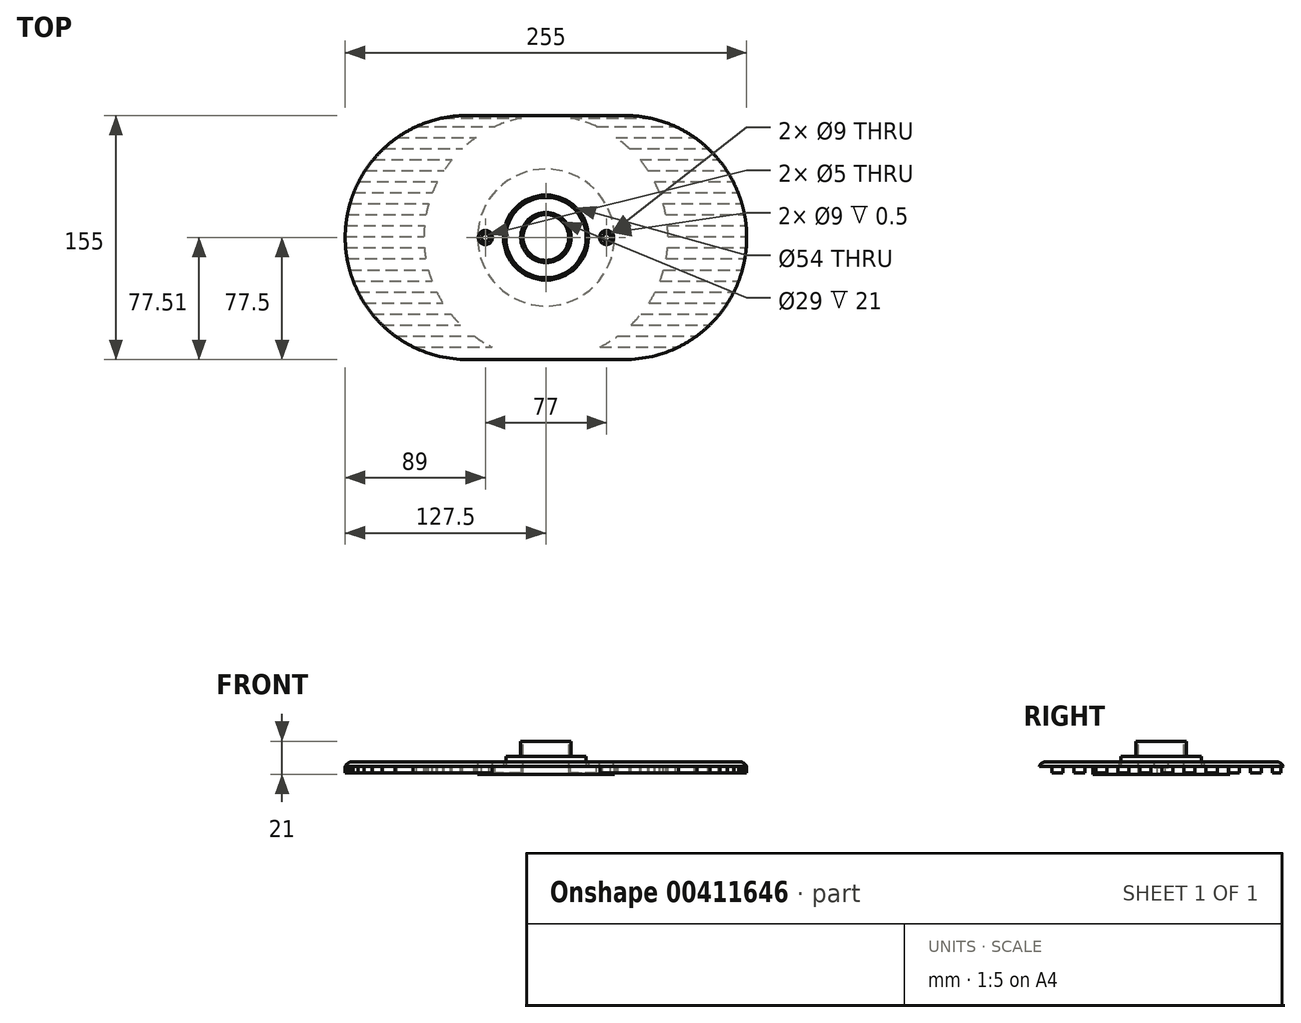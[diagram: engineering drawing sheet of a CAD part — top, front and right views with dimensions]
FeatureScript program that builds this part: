
annotation { "Feature Type Name" : "Feature", "Feature Type Description" : "" }
export const myFeature = defineFeature(function(context is Context, id is Id, definition is map)
    precondition{}
    {
        {
            var Q0;
            Q0=qCreatedBy(makeId("Top.planeOp"),FACE);
            var sketch = newSketch(context, id + "F0", { "sketchPlane" : qUnion([Q0])});
            skCircle(sketch, "E0", {"center": v(0, 0) * mm, "radius": 25.5 * mm});
            skCircle(sketch, "E1", {"center": v(0, 0.01) * mm, "radius": 14.5 * mm});
            skCircle(sketch, "E2", {"center": v(0, 0) * mm, "radius": 77.5 * mm});
            skCircle(sketch, "E3", {"center": v(0, 0) * mm, "radius": 16 * mm});
            skLineSegment(sketch, "E4", {"start": v(0, 77.5) * mm, "end": v(50, 77.5) * mm});
            skLineSegment(sketch, "E5", {"start": v(0, 77.5) * mm, "end": v(-50, 77.5) * mm});
            skLineSegment(sketch, "E6", {"start": v(0, -77.5) * mm, "end": v(-50, -77.5) * mm});
            skLineSegment(sketch, "E7", {"start": v(0, -77.5) * mm, "end": v(50, -77.5) * mm});
            skArc(sketch, "E8", {"start": v(-50, 77.5) * mm, "mid": v(-127.5, 0) * mm, "end": v(-50, -77.5) * mm});
            skLineSegment(sketch, "E9", {"start": v(0, 0) * mm, "end": v(0, 99.89) * mm, "construction": true});
            skArc(sketch, "E10.MirrorCS", {"start": v(50, 77.5) * mm, "mid": v(127.5, 0) * mm, "end": v(50, -77.5) * mm});
            skCircle(sketch, "E11", {"center": v(0, 0.01) * mm, "radius": 27 * mm});
            skEllipse(sketch, "E12", {"center": v(0, 0.01) * mm, "majorRadius": 43.5 * mm, "minorRadius": 43.5 * mm, "majorAxis": v(-1, 0)});
            skLineSegment(sketch, "E13.0.1.0", {"start": v(-94.43, 63.5) * mm, "end": v(-44.43, 63.5) * mm});
            skLineSegment(sketch, "E13.0.2.0", {"start": v(-103.05, 56.5) * mm, "end": v(-53.05, 56.5) * mm});
            skLineSegment(sketch, "E13.0.3.0", {"start": v(-109.63, 49.5) * mm, "end": v(-59.63, 49.5) * mm});
            skLineSegment(sketch, "E13.0.4.0", {"start": v(-114.8, 42.5) * mm, "end": v(-64.8, 42.5) * mm});
            skLineSegment(sketch, "E13.0.5.0", {"start": v(-118.9, 35.5) * mm, "end": v(-68.9, 35.5) * mm});
            skLineSegment(sketch, "E13.0.6.0", {"start": v(-122.07, 28.5) * mm, "end": v(-72.07, 28.5) * mm});
            skLineSegment(sketch, "E13.0.7.0", {"start": v(-124.46, 21.5) * mm, "end": v(-74.46, 21.5) * mm});
            skLineSegment(sketch, "E13.0.8.0", {"start": v(-126.13, 14.5) * mm, "end": v(-76.13, 14.5) * mm});
            skLineSegment(sketch, "E13.0.9.0", {"start": v(-127.14, 7.5) * mm, "end": v(-77.14, 7.5) * mm});
            skLineSegment(sketch, "E13.0.10.0", {"start": v(-127.5, 0.5) * mm, "end": v(-77.5, 0.5) * mm});
            skLineSegment(sketch, "E13.0.11.0", {"start": v(-127.23, -6.5) * mm, "end": v(-77.23, -6.5) * mm});
            skLineSegment(sketch, "E13.0.12.0", {"start": v(-126.32, -13.5) * mm, "end": v(-76.32, -13.5) * mm});
            skLineSegment(sketch, "E13.0.13.0", {"start": v(-124.74, -20.5) * mm, "end": v(-74.74, -20.5) * mm});
            skLineSegment(sketch, "E13.0.14.0", {"start": v(-122.46, -27.5) * mm, "end": v(-72.46, -27.5) * mm});
            skLineSegment(sketch, "E13.0.15.0", {"start": v(-119.4, -34.5) * mm, "end": v(-69.4, -34.5) * mm});
            skLineSegment(sketch, "E13.0.16.0", {"start": v(-115.45, -41.5) * mm, "end": v(-65.45, -41.5) * mm});
            skLineSegment(sketch, "E13.0.17.0", {"start": v(-110.45, -48.5) * mm, "end": v(-60.45, -48.5) * mm});
            skLineSegment(sketch, "E13.0.18.0", {"start": v(-104.1, -55.5) * mm, "end": v(-54.1, -55.5) * mm});
            skLineSegment(sketch, "E13.0.19.0", {"start": v(-95.83, -62.5) * mm, "end": v(-45.83, -62.5) * mm});
            skLineSegment(sketch, "E13.0.20.0", {"start": v(-84.3, -69.5) * mm, "end": v(-34.3, -69.5) * mm});
            skLineSegment(sketch, "E14.trimOffspring", {"start": v(32.19, 70.5) * mm, "end": v(82.19, 70.5) * mm});
            skLineSegment(sketch, "E15.trimOffspring", {"start": v(44.43, 63.5) * mm, "end": v(94.43, 63.5) * mm});
            skLineSegment(sketch, "E16.trimOffspring", {"start": v(53.05, 56.5) * mm, "end": v(103.05, 56.5) * mm});
            skLineSegment(sketch, "E17.trimOffspring", {"start": v(59.63, 49.5) * mm, "end": v(109.63, 49.5) * mm});
            skLineSegment(sketch, "E18.trimOffspring", {"start": v(64.8, 42.5) * mm, "end": v(114.8, 42.5) * mm});
            skLineSegment(sketch, "E19.trimOffspring", {"start": v(68.9, 35.5) * mm, "end": v(118.9, 35.5) * mm});
            skLineSegment(sketch, "E20.trimOffspring", {"start": v(72.07, 28.5) * mm, "end": v(122.07, 28.5) * mm});
            skLineSegment(sketch, "E21.trimOffspring", {"start": v(74.46, 21.5) * mm, "end": v(124.46, 21.5) * mm});
            skLineSegment(sketch, "E22.trimOffspring", {"start": v(76.13, 14.5) * mm, "end": v(126.13, 14.5) * mm});
            skLineSegment(sketch, "E23.trimOffspring", {"start": v(77.14, 7.5) * mm, "end": v(127.14, 7.5) * mm});
            skLineSegment(sketch, "E24.trimOffspring", {"start": v(77.5, 0.5) * mm, "end": v(127.5, 0.5) * mm});
            skLineSegment(sketch, "E25.trimOffspring", {"start": v(77.23, -6.5) * mm, "end": v(127.23, -6.5) * mm});
            skLineSegment(sketch, "E26.trimOffspring", {"start": v(76.32, -13.5) * mm, "end": v(126.32, -13.5) * mm});
            skLineSegment(sketch, "E27.trimOffspring", {"start": v(74.74, -20.5) * mm, "end": v(124.74, -20.5) * mm});
            skLineSegment(sketch, "E28.trimOffspring", {"start": v(72.46, -27.5) * mm, "end": v(122.46, -27.5) * mm});
            skLineSegment(sketch, "E29.trimOffspring", {"start": v(69.4, -34.5) * mm, "end": v(119.4, -34.5) * mm});
            skLineSegment(sketch, "E30.trimOffspring", {"start": v(65.45, -41.5) * mm, "end": v(115.45, -41.5) * mm});
            skLineSegment(sketch, "E31.trimOffspring", {"start": v(60.45, -48.5) * mm, "end": v(110.45, -48.5) * mm});
            skLineSegment(sketch, "E32.trimOffspring", {"start": v(54.1, -55.5) * mm, "end": v(104.1, -55.5) * mm});
            skLineSegment(sketch, "E33.trimOffspring", {"start": v(45.83, -62.5) * mm, "end": v(95.83, -62.5) * mm});
            skLineSegment(sketch, "E34.trimOffspring", {"start": v(34.3, -69.5) * mm, "end": v(84.3, -69.5) * mm});
            skLineSegment(sketch, "E35.trimOffspring", {"start": v(-82.19, 70.5) * mm, "end": v(-32.19, 70.5) * mm});
            skLineSegment(sketch, "E36", {"start": v(-65.46, 75.94) * mm, "end": v(-15.46, 75.94) * mm});
            skLineSegment(sketch, "E37.trimOffspring", {"start": v(15.46, 75.94) * mm, "end": v(65.46, 75.94) * mm});
            skLineSegment(sketch, "E38", {"start": v(0, 0.01) * mm, "end": v(-38.5, 0.01) * mm, "construction": true});
            skLineSegment(sketch, "E39", {"start": v(0, 0.01) * mm, "end": v(38.5, 0.01) * mm, "construction": true});
            skSolve(sketch);
        }
        {
            var Q0;
            Q0=makeQuery(id+"F0.imprint","IMPRINT",FACE,{"disambiguationData":[TD([[makeQuery(id+"F0.imprint","IMPRINT",EDGE,{"derivedFrom":sQuery(id+"F0.wireOp",EDGE,"E11")}),-1.0]])]});
            var Q1;
            Q1=makeQuery(id+"F0.imprint","IMPRINT",FACE,{"disambiguationData":[TD([[makeQuery(id+"F0.imprint","IMPRINT",EDGE,{"derivedFrom":sQuery(id+"F0.wireOp",EDGE,"E0")}),-1.0]])]});
            var Q2;
            Q2=makeQuery(id+"F0.imprint","IMPRINT",FACE,{"disambiguationData":[TD([[makeQuery(id+"F0.imprint","IMPRINT",EDGE,{"derivedFrom":sQuery(id+"F0.wireOp",EDGE,"E0")}),1.0]])]});
            var Q3;
            Q3=makeQuery(id+"F0.imprint","IMPRINT",FACE,{"disambiguationData":[TD([[makeQuery(id+"F0.imprint","IMPRINT",EDGE,{"derivedFrom":sQuery(id+"F0.wireOp",EDGE,"E1")}),-1.0]])]});
            extrude(context, id + "F1", {"entities" : qUnion([Q0, Q1, Q2, Q3]), "oppositeDirection" : true, "depth" : 5 * mm});
        }
        {
            var Q0;
            Q0=makeQuery(id+"F0.imprint","IMPRINT",FACE,{"disambiguationData":[TD([[makeQuery(id+"F0.imprint","IMPRINT",EDGE,{"derivedFrom":sQuery(id+"F0.wireOp",EDGE,"E0")}),1.0]])]});
            extrude(context, id + "F2", {"entities" : qUnion([Q0]), "operationType" : NewBodyOperationType.ADD, "depth" : 6.5 * mm});
        }
        {
            var Q0;
            Q0=makeQuery(id+"F0.imprint","IMPRINT",FACE,{"disambiguationData":[TD([[makeQuery(id+"F0.imprint","IMPRINT",EDGE,{"derivedFrom":sQuery(id+"F0.wireOp",EDGE,"E1")}),-1.0]])]});
            extrude(context, id + "F3", {"entities" : qUnion([Q0]), "operationType" : NewBodyOperationType.ADD, "depth" : 16 * mm});
        }
        {
            var Q0;
            Q0=makeQuery(id+"F0.imprint","IMPRINT",FACE,{"disambiguationData":[TD([[makeQuery(id+"F0.imprint","IMPRINT",EDGE,{"derivedFrom":sQuery(id+"F0.wireOp",EDGE,"E12")}),-1.0]])]});
            var Q1;
            Q1=makeQuery(id+"F0.imprint","IMPRINT",FACE,{"disambiguationData":[TD([[makeQuery(id+"F0.imprint","IMPRINT",EDGE,{"derivedFrom":sQuery(id+"F0.wireOp",EDGE,"E11")}),-1.0]])]});
            var Q2;
            {var subQ0=sQuery(id+"F0.wireOp",EDGE,"E5");Q2=makeQuery(id+"F0.imprint","IMPRINT",FACE,{"disambiguationData":[TD([[makeQuery(id+"F0.imprint","IMPRINT",EDGE,{"derivedFrom":subQ0}),1.0]])]});}
            var Q3;
            {var subQ0=sQuery(id+"F0.wireOp",EDGE,"E13.0.1.0");Q3=makeQuery(id+"F0.imprint","IMPRINT",FACE,{"disambiguationData":[TD([[makeQuery(id+"F0.imprint","IMPRINT",EDGE,{"derivedFrom":subQ0}),1.0]])]});}
            var Q4;
            {var subQ0=sQuery(id+"F0.wireOp",EDGE,"E13.0.1.0");Q4=makeQuery(id+"F0.imprint","IMPRINT",FACE,{"disambiguationData":[TD([[makeQuery(id+"F0.imprint","IMPRINT",EDGE,{"derivedFrom":subQ0}),-1.0]])]});}
            var Q5;
            {var subQ0=sQuery(id+"F0.wireOp",EDGE,"E13.0.2.0");Q5=makeQuery(id+"F0.imprint","IMPRINT",FACE,{"disambiguationData":[TD([[makeQuery(id+"F0.imprint","IMPRINT",EDGE,{"derivedFrom":subQ0}),-1.0]])]});}
            var Q6;
            {var subQ0=sQuery(id+"F0.wireOp",EDGE,"E13.0.3.0");Q6=makeQuery(id+"F0.imprint","IMPRINT",FACE,{"disambiguationData":[TD([[makeQuery(id+"F0.imprint","IMPRINT",EDGE,{"derivedFrom":subQ0}),-1.0]])]});}
            var Q7;
            {var subQ0=sQuery(id+"F0.wireOp",EDGE,"E13.0.4.0");Q7=makeQuery(id+"F0.imprint","IMPRINT",FACE,{"disambiguationData":[TD([[makeQuery(id+"F0.imprint","IMPRINT",EDGE,{"derivedFrom":subQ0}),-1.0]])]});}
            var Q8;
            {var subQ0=sQuery(id+"F0.wireOp",EDGE,"E13.0.5.0");Q8=makeQuery(id+"F0.imprint","IMPRINT",FACE,{"disambiguationData":[TD([[makeQuery(id+"F0.imprint","IMPRINT",EDGE,{"derivedFrom":subQ0}),-1.0]])]});}
            var Q9;
            {var subQ0=sQuery(id+"F0.wireOp",EDGE,"E13.0.6.0");Q9=makeQuery(id+"F0.imprint","IMPRINT",FACE,{"disambiguationData":[TD([[makeQuery(id+"F0.imprint","IMPRINT",EDGE,{"derivedFrom":subQ0}),-1.0]])]});}
            var Q10;
            {var subQ0=sQuery(id+"F0.wireOp",EDGE,"E13.0.7.0");Q10=makeQuery(id+"F0.imprint","IMPRINT",FACE,{"disambiguationData":[TD([[makeQuery(id+"F0.imprint","IMPRINT",EDGE,{"derivedFrom":subQ0}),-1.0]])]});}
            var Q11;
            {var subQ0=sQuery(id+"F0.wireOp",EDGE,"E13.0.8.0");Q11=makeQuery(id+"F0.imprint","IMPRINT",FACE,{"disambiguationData":[TD([[makeQuery(id+"F0.imprint","IMPRINT",EDGE,{"derivedFrom":subQ0}),-1.0]])]});}
            var Q12;
            {var subQ0=sQuery(id+"F0.wireOp",EDGE,"E13.0.9.0");Q12=makeQuery(id+"F0.imprint","IMPRINT",FACE,{"disambiguationData":[TD([[makeQuery(id+"F0.imprint","IMPRINT",EDGE,{"derivedFrom":subQ0}),-1.0]])]});}
            var Q13;
            {var subQ0=sQuery(id+"F0.wireOp",EDGE,"E13.0.10.0");Q13=makeQuery(id+"F0.imprint","IMPRINT",FACE,{"disambiguationData":[TD([[makeQuery(id+"F0.imprint","IMPRINT",EDGE,{"derivedFrom":subQ0}),-1.0]])]});}
            var Q14;
            {var subQ0=sQuery(id+"F0.wireOp",EDGE,"E13.0.11.0");Q14=makeQuery(id+"F0.imprint","IMPRINT",FACE,{"disambiguationData":[TD([[makeQuery(id+"F0.imprint","IMPRINT",EDGE,{"derivedFrom":subQ0}),-1.0]])]});}
            var Q15;
            {var subQ0=sQuery(id+"F0.wireOp",EDGE,"E13.0.12.0");Q15=makeQuery(id+"F0.imprint","IMPRINT",FACE,{"disambiguationData":[TD([[makeQuery(id+"F0.imprint","IMPRINT",EDGE,{"derivedFrom":subQ0}),-1.0]])]});}
            var Q16;
            {var subQ0=sQuery(id+"F0.wireOp",EDGE,"E13.0.13.0");Q16=makeQuery(id+"F0.imprint","IMPRINT",FACE,{"disambiguationData":[TD([[makeQuery(id+"F0.imprint","IMPRINT",EDGE,{"derivedFrom":subQ0}),-1.0]])]});}
            var Q17;
            {var subQ0=sQuery(id+"F0.wireOp",EDGE,"E13.0.15.0");Q17=makeQuery(id+"F0.imprint","IMPRINT",FACE,{"disambiguationData":[TD([[makeQuery(id+"F0.imprint","IMPRINT",EDGE,{"derivedFrom":subQ0}),-1.0]])]});}
            var Q18;
            {var subQ0=sQuery(id+"F0.wireOp",EDGE,"E13.0.16.0");Q18=makeQuery(id+"F0.imprint","IMPRINT",FACE,{"disambiguationData":[TD([[makeQuery(id+"F0.imprint","IMPRINT",EDGE,{"derivedFrom":subQ0}),-1.0]])]});}
            var Q19;
            {var subQ0=sQuery(id+"F0.wireOp",EDGE,"E13.0.17.0");Q19=makeQuery(id+"F0.imprint","IMPRINT",FACE,{"disambiguationData":[TD([[makeQuery(id+"F0.imprint","IMPRINT",EDGE,{"derivedFrom":subQ0}),-1.0]])]});}
            var Q20;
            {var subQ0=sQuery(id+"F0.wireOp",EDGE,"E13.0.18.0");Q20=makeQuery(id+"F0.imprint","IMPRINT",FACE,{"disambiguationData":[TD([[makeQuery(id+"F0.imprint","IMPRINT",EDGE,{"derivedFrom":subQ0}),-1.0]])]});}
            var Q21;
            {var subQ0=sQuery(id+"F0.wireOp",EDGE,"E13.0.19.0");Q21=makeQuery(id+"F0.imprint","IMPRINT",FACE,{"disambiguationData":[TD([[makeQuery(id+"F0.imprint","IMPRINT",EDGE,{"derivedFrom":subQ0}),-1.0]])]});}
            var Q22;
            {var subQ0=sQuery(id+"F0.wireOp",EDGE,"E6");Q22=makeQuery(id+"F0.imprint","IMPRINT",FACE,{"disambiguationData":[TD([[makeQuery(id+"F0.imprint","IMPRINT",EDGE,{"derivedFrom":subQ0}),-1.0]])]});}
            var Q23;
            {var subQ0=sQuery(id+"F0.wireOp",EDGE,"E13.0.14.0");Q23=makeQuery(id+"F0.imprint","IMPRINT",FACE,{"disambiguationData":[TD([[makeQuery(id+"F0.imprint","IMPRINT",EDGE,{"derivedFrom":subQ0}),-1.0]])]});}
            var Q24;
            {var subQ0=sQuery(id+"F0.wireOp",EDGE,"E7");Q24=makeQuery(id+"F0.imprint","IMPRINT",FACE,{"disambiguationData":[TD([[makeQuery(id+"F0.imprint","IMPRINT",EDGE,{"derivedFrom":subQ0}),1.0]])]});}
            var Q25;
            {var subQ0=sQuery(id+"F0.wireOp",EDGE,"E33.trimOffspring");Q25=makeQuery(id+"F0.imprint","IMPRINT",FACE,{"disambiguationData":[TD([[makeQuery(id+"F0.imprint","IMPRINT",EDGE,{"derivedFrom":subQ0}),-1.0]])]});}
            var Q26;
            {var subQ0=sQuery(id+"F0.wireOp",EDGE,"E32.trimOffspring");Q26=makeQuery(id+"F0.imprint","IMPRINT",FACE,{"disambiguationData":[TD([[makeQuery(id+"F0.imprint","IMPRINT",EDGE,{"derivedFrom":subQ0}),-1.0]])]});}
            var Q27;
            {var subQ0=sQuery(id+"F0.wireOp",EDGE,"E31.trimOffspring");Q27=makeQuery(id+"F0.imprint","IMPRINT",FACE,{"disambiguationData":[TD([[makeQuery(id+"F0.imprint","IMPRINT",EDGE,{"derivedFrom":subQ0}),-1.0]])]});}
            var Q28;
            {var subQ0=sQuery(id+"F0.wireOp",EDGE,"E30.trimOffspring");Q28=makeQuery(id+"F0.imprint","IMPRINT",FACE,{"disambiguationData":[TD([[makeQuery(id+"F0.imprint","IMPRINT",EDGE,{"derivedFrom":subQ0}),-1.0]])]});}
            var Q29;
            {var subQ0=sQuery(id+"F0.wireOp",EDGE,"E29.trimOffspring");Q29=makeQuery(id+"F0.imprint","IMPRINT",FACE,{"disambiguationData":[TD([[makeQuery(id+"F0.imprint","IMPRINT",EDGE,{"derivedFrom":subQ0}),-1.0]])]});}
            var Q30;
            {var subQ0=sQuery(id+"F0.wireOp",EDGE,"E28.trimOffspring");Q30=makeQuery(id+"F0.imprint","IMPRINT",FACE,{"disambiguationData":[TD([[makeQuery(id+"F0.imprint","IMPRINT",EDGE,{"derivedFrom":subQ0}),-1.0]])]});}
            var Q31;
            {var subQ0=sQuery(id+"F0.wireOp",EDGE,"E27.trimOffspring");Q31=makeQuery(id+"F0.imprint","IMPRINT",FACE,{"disambiguationData":[TD([[makeQuery(id+"F0.imprint","IMPRINT",EDGE,{"derivedFrom":subQ0}),-1.0]])]});}
            var Q32;
            {var subQ0=sQuery(id+"F0.wireOp",EDGE,"E26.trimOffspring");Q32=makeQuery(id+"F0.imprint","IMPRINT",FACE,{"disambiguationData":[TD([[makeQuery(id+"F0.imprint","IMPRINT",EDGE,{"derivedFrom":subQ0}),-1.0]])]});}
            var Q33;
            {var subQ0=sQuery(id+"F0.wireOp",EDGE,"E25.trimOffspring");Q33=makeQuery(id+"F0.imprint","IMPRINT",FACE,{"disambiguationData":[TD([[makeQuery(id+"F0.imprint","IMPRINT",EDGE,{"derivedFrom":subQ0}),-1.0]])]});}
            var Q34;
            {var subQ0=sQuery(id+"F0.wireOp",EDGE,"E24.trimOffspring");Q34=makeQuery(id+"F0.imprint","IMPRINT",FACE,{"disambiguationData":[TD([[makeQuery(id+"F0.imprint","IMPRINT",EDGE,{"derivedFrom":subQ0}),-1.0]])]});}
            var Q35;
            {var subQ0=sQuery(id+"F0.wireOp",EDGE,"E23.trimOffspring");Q35=makeQuery(id+"F0.imprint","IMPRINT",FACE,{"disambiguationData":[TD([[makeQuery(id+"F0.imprint","IMPRINT",EDGE,{"derivedFrom":subQ0}),-1.0]])]});}
            var Q36;
            {var subQ0=sQuery(id+"F0.wireOp",EDGE,"E22.trimOffspring");Q36=makeQuery(id+"F0.imprint","IMPRINT",FACE,{"disambiguationData":[TD([[makeQuery(id+"F0.imprint","IMPRINT",EDGE,{"derivedFrom":subQ0}),-1.0]])]});}
            var Q37;
            {var subQ0=sQuery(id+"F0.wireOp",EDGE,"E21.trimOffspring");Q37=makeQuery(id+"F0.imprint","IMPRINT",FACE,{"disambiguationData":[TD([[makeQuery(id+"F0.imprint","IMPRINT",EDGE,{"derivedFrom":subQ0}),-1.0]])]});}
            var Q38;
            {var subQ0=sQuery(id+"F0.wireOp",EDGE,"E20.trimOffspring");Q38=makeQuery(id+"F0.imprint","IMPRINT",FACE,{"disambiguationData":[TD([[makeQuery(id+"F0.imprint","IMPRINT",EDGE,{"derivedFrom":subQ0}),-1.0]])]});}
            var Q39;
            {var subQ0=sQuery(id+"F0.wireOp",EDGE,"E19.trimOffspring");Q39=makeQuery(id+"F0.imprint","IMPRINT",FACE,{"disambiguationData":[TD([[makeQuery(id+"F0.imprint","IMPRINT",EDGE,{"derivedFrom":subQ0}),-1.0]])]});}
            var Q40;
            {var subQ0=sQuery(id+"F0.wireOp",EDGE,"E18.trimOffspring");Q40=makeQuery(id+"F0.imprint","IMPRINT",FACE,{"disambiguationData":[TD([[makeQuery(id+"F0.imprint","IMPRINT",EDGE,{"derivedFrom":subQ0}),-1.0]])]});}
            var Q41;
            {var subQ0=sQuery(id+"F0.wireOp",EDGE,"E17.trimOffspring");Q41=makeQuery(id+"F0.imprint","IMPRINT",FACE,{"disambiguationData":[TD([[makeQuery(id+"F0.imprint","IMPRINT",EDGE,{"derivedFrom":subQ0}),-1.0]])]});}
            var Q42;
            {var subQ0=sQuery(id+"F0.wireOp",EDGE,"E4");Q42=makeQuery(id+"F0.imprint","IMPRINT",FACE,{"disambiguationData":[TD([[makeQuery(id+"F0.imprint","IMPRINT",EDGE,{"derivedFrom":subQ0}),-1.0]])]});}
            var Q43;
            {var subQ0=sQuery(id+"F0.wireOp",EDGE,"E14.trimOffspring");Q43=makeQuery(id+"F0.imprint","IMPRINT",FACE,{"disambiguationData":[TD([[makeQuery(id+"F0.imprint","IMPRINT",EDGE,{"derivedFrom":subQ0}),-1.0]])]});}
            var Q44;
            {var subQ0=sQuery(id+"F0.wireOp",EDGE,"E15.trimOffspring");Q44=makeQuery(id+"F0.imprint","IMPRINT",FACE,{"disambiguationData":[TD([[makeQuery(id+"F0.imprint","IMPRINT",EDGE,{"derivedFrom":subQ0}),-1.0]])]});}
            var Q45;
            {var subQ0=sQuery(id+"F0.wireOp",EDGE,"E16.trimOffspring");Q45=makeQuery(id+"F0.imprint","IMPRINT",FACE,{"disambiguationData":[TD([[makeQuery(id+"F0.imprint","IMPRINT",EDGE,{"derivedFrom":subQ0}),-1.0]])]});}
            var Q46;
            {var subQ0=sQuery(id+"F0.wireOp",EDGE,"E35.trimOffspring");Q46=makeQuery(id+"F0.imprint","IMPRINT",FACE,{"disambiguationData":[TD([[makeQuery(id+"F0.imprint","IMPRINT",EDGE,{"derivedFrom":subQ0}),1.0]])]});}
            var Q47;
            {var subQ0=sQuery(id+"F0.wireOp",EDGE,"E14.trimOffspring");Q47=makeQuery(id+"F0.imprint","IMPRINT",FACE,{"disambiguationData":[TD([[makeQuery(id+"F0.imprint","IMPRINT",EDGE,{"derivedFrom":subQ0}),1.0]])]});}
            extrude(context, id + "F4", {"entities" : qUnion([Q0, Q1, Q2, Q3, Q4, Q5, Q6, Q7, Q8, Q9, Q10, Q11, Q12, Q13, Q14, Q15, Q16, Q17, Q18, Q19, Q20, Q21, Q22, Q23, Q24, Q25, Q26, Q27, Q28, Q29, Q30, Q31, Q32, Q33, Q34, Q35, Q36, Q37, Q38, Q39, Q40, Q41, Q42, Q43, Q44, Q45, Q46, Q47]), "depth" : 3 * mm});
        }
        {
            var Q0;
            Q0=makeQuery(id+"F4.opExtrude","CAP_EDGE",EDGE,{"disambiguationData":[OSD([sQuery(id+"F0.wireOp",EDGE,"E6"),sQuery(id+"F0.wireOp",EDGE,"E7")])],"isStart":false});
            fillet(context, id + "F5", {"entities" : qUnion([Q0]), "radius" : 5 * mm, "tangentPropagation" : true, "allowEdgeOverflow" : false});
        }
        {
            var Q0;
            {var subQ0=sQuery(id+"F0.wireOp",EDGE,"E13.0.19.0");Q0=makeQuery(id+"F0.imprint","IMPRINT",FACE,{"disambiguationData":[TD([[makeQuery(id+"F0.imprint","IMPRINT",EDGE,{"derivedFrom":subQ0}),-1.0]])]});}
            var Q1;
            {var subQ0=sQuery(id+"F0.wireOp",EDGE,"E13.0.17.0");Q1=makeQuery(id+"F0.imprint","IMPRINT",FACE,{"disambiguationData":[TD([[makeQuery(id+"F0.imprint","IMPRINT",EDGE,{"derivedFrom":subQ0}),-1.0]])]});}
            var Q2;
            {var subQ0=sQuery(id+"F0.wireOp",EDGE,"E13.0.15.0");Q2=makeQuery(id+"F0.imprint","IMPRINT",FACE,{"disambiguationData":[TD([[makeQuery(id+"F0.imprint","IMPRINT",EDGE,{"derivedFrom":subQ0}),-1.0]])]});}
            var Q3;
            {var subQ0=sQuery(id+"F0.wireOp",EDGE,"E13.0.13.0");Q3=makeQuery(id+"F0.imprint","IMPRINT",FACE,{"disambiguationData":[TD([[makeQuery(id+"F0.imprint","IMPRINT",EDGE,{"derivedFrom":subQ0}),-1.0]])]});}
            var Q4;
            {var subQ0=sQuery(id+"F0.wireOp",EDGE,"E13.0.11.0");Q4=makeQuery(id+"F0.imprint","IMPRINT",FACE,{"disambiguationData":[TD([[makeQuery(id+"F0.imprint","IMPRINT",EDGE,{"derivedFrom":subQ0}),-1.0]])]});}
            var Q5;
            {var subQ0=sQuery(id+"F0.wireOp",EDGE,"E13.0.9.0");Q5=makeQuery(id+"F0.imprint","IMPRINT",FACE,{"disambiguationData":[TD([[makeQuery(id+"F0.imprint","IMPRINT",EDGE,{"derivedFrom":subQ0}),-1.0]])]});}
            var Q6;
            {var subQ0=sQuery(id+"F0.wireOp",EDGE,"E13.0.7.0");Q6=makeQuery(id+"F0.imprint","IMPRINT",FACE,{"disambiguationData":[TD([[makeQuery(id+"F0.imprint","IMPRINT",EDGE,{"derivedFrom":subQ0}),-1.0]])]});}
            var Q7;
            {var subQ0=sQuery(id+"F0.wireOp",EDGE,"E13.0.5.0");Q7=makeQuery(id+"F0.imprint","IMPRINT",FACE,{"disambiguationData":[TD([[makeQuery(id+"F0.imprint","IMPRINT",EDGE,{"derivedFrom":subQ0}),-1.0]])]});}
            var Q8;
            {var subQ0=sQuery(id+"F0.wireOp",EDGE,"E13.0.3.0");Q8=makeQuery(id+"F0.imprint","IMPRINT",FACE,{"disambiguationData":[TD([[makeQuery(id+"F0.imprint","IMPRINT",EDGE,{"derivedFrom":subQ0}),-1.0]])]});}
            var Q9;
            {var subQ0=sQuery(id+"F0.wireOp",EDGE,"E13.0.1.0");Q9=makeQuery(id+"F0.imprint","IMPRINT",FACE,{"disambiguationData":[TD([[makeQuery(id+"F0.imprint","IMPRINT",EDGE,{"derivedFrom":subQ0}),-1.0]])]});}
            var Q10;
            {var subQ0=sQuery(id+"F0.wireOp",EDGE,"E15.trimOffspring");Q10=makeQuery(id+"F0.imprint","IMPRINT",FACE,{"disambiguationData":[TD([[makeQuery(id+"F0.imprint","IMPRINT",EDGE,{"derivedFrom":subQ0}),-1.0]])]});}
            var Q11;
            {var subQ0=sQuery(id+"F0.wireOp",EDGE,"E17.trimOffspring");Q11=makeQuery(id+"F0.imprint","IMPRINT",FACE,{"disambiguationData":[TD([[makeQuery(id+"F0.imprint","IMPRINT",EDGE,{"derivedFrom":subQ0}),-1.0]])]});}
            var Q12;
            {var subQ0=sQuery(id+"F0.wireOp",EDGE,"E19.trimOffspring");Q12=makeQuery(id+"F0.imprint","IMPRINT",FACE,{"disambiguationData":[TD([[makeQuery(id+"F0.imprint","IMPRINT",EDGE,{"derivedFrom":subQ0}),-1.0]])]});}
            var Q13;
            {var subQ0=sQuery(id+"F0.wireOp",EDGE,"E21.trimOffspring");Q13=makeQuery(id+"F0.imprint","IMPRINT",FACE,{"disambiguationData":[TD([[makeQuery(id+"F0.imprint","IMPRINT",EDGE,{"derivedFrom":subQ0}),-1.0]])]});}
            var Q14;
            {var subQ0=sQuery(id+"F0.wireOp",EDGE,"E25.trimOffspring");Q14=makeQuery(id+"F0.imprint","IMPRINT",FACE,{"disambiguationData":[TD([[makeQuery(id+"F0.imprint","IMPRINT",EDGE,{"derivedFrom":subQ0}),-1.0]])]});}
            var Q15;
            {var subQ0=sQuery(id+"F0.wireOp",EDGE,"E23.trimOffspring");Q15=makeQuery(id+"F0.imprint","IMPRINT",FACE,{"disambiguationData":[TD([[makeQuery(id+"F0.imprint","IMPRINT",EDGE,{"derivedFrom":subQ0}),-1.0]])]});}
            var Q16;
            {var subQ0=sQuery(id+"F0.wireOp",EDGE,"E27.trimOffspring");Q16=makeQuery(id+"F0.imprint","IMPRINT",FACE,{"disambiguationData":[TD([[makeQuery(id+"F0.imprint","IMPRINT",EDGE,{"derivedFrom":subQ0}),-1.0]])]});}
            var Q17;
            {var subQ0=sQuery(id+"F0.wireOp",EDGE,"E29.trimOffspring");Q17=makeQuery(id+"F0.imprint","IMPRINT",FACE,{"disambiguationData":[TD([[makeQuery(id+"F0.imprint","IMPRINT",EDGE,{"derivedFrom":subQ0}),-1.0]])]});}
            var Q18;
            {var subQ0=sQuery(id+"F0.wireOp",EDGE,"E31.trimOffspring");Q18=makeQuery(id+"F0.imprint","IMPRINT",FACE,{"disambiguationData":[TD([[makeQuery(id+"F0.imprint","IMPRINT",EDGE,{"derivedFrom":subQ0}),-1.0]])]});}
            var Q19;
            {var subQ0=sQuery(id+"F0.wireOp",EDGE,"E33.trimOffspring");Q19=makeQuery(id+"F0.imprint","IMPRINT",FACE,{"disambiguationData":[TD([[makeQuery(id+"F0.imprint","IMPRINT",EDGE,{"derivedFrom":subQ0}),-1.0]])]});}
            var Q20;
            {var subQ0=sQuery(id+"F0.wireOp",EDGE,"E35.trimOffspring");Q20=makeQuery(id+"F0.imprint","IMPRINT",FACE,{"disambiguationData":[TD([[makeQuery(id+"F0.imprint","IMPRINT",EDGE,{"derivedFrom":subQ0}),1.0]])]});}
            var Q21;
            {var subQ0=sQuery(id+"F0.wireOp",EDGE,"E14.trimOffspring");Q21=makeQuery(id+"F0.imprint","IMPRINT",FACE,{"disambiguationData":[TD([[makeQuery(id+"F0.imprint","IMPRINT",EDGE,{"derivedFrom":subQ0}),1.0]])]});}
            extrude(context, id + "F6", {"entities" : qUnion([Q0, Q1, Q2, Q3, Q4, Q5, Q6, Q7, Q8, Q9, Q10, Q11, Q12, Q13, Q14, Q15, Q16, Q17, Q18, Q19, Q20, Q21]), "operationType" : NewBodyOperationType.ADD, "oppositeDirection" : true, "depth" : 4 * mm});
        }
        {
            var Q0;
            Q0=makeQuery(id+"F4.opExtrude","CAP_FACE",FACE,{"disambiguationData":[OSD([sQuery(id+"F0.wireOp",EDGE,"E4"),sQuery(id+"F0.wireOp",EDGE,"E5"),sQuery(id+"F0.wireOp",EDGE,"E6"),sQuery(id+"F0.wireOp",EDGE,"E7"),sQuery(id+"F0.wireOp",EDGE,"E8"),sQuery(id+"F0.wireOp",EDGE,"E10.MirrorCS"),sQuery(id+"F0.wireOp",EDGE,"E11")])],"isStart":false});
            var sketch = newSketch(context, id + "F7", { "sketchPlane" : qUnion([Q0])});
            skLineSegment(sketch, "E40", {"start": v(0, 0) * mm, "end": v(-38.5, 0) * mm, "construction": true});
            skLineSegment(sketch, "E41", {"start": v(0, 0) * mm, "end": v(38.5, 0) * mm, "construction": true});
            skSolve(sketch);
        }
        {
            var Q0;
            Q0=sQuery(id+"F7.wireOp",VERTEX,"E40.end");
            var Q1;
            Q1=sQuery(id+"F7.wireOp",VERTEX,"E41.end");
            var Q2;
            Q2=makeQuery(id+"F1.opExtrude","SWEPT_BODY",BODY,{"disambiguationData":[OSD([sQuery(id+"F0.wireOp",EDGE,"E1"),sQuery(id+"F0.wireOp",EDGE,"E12")])]});
            var Q3;
            Q3=makeQuery(id+"F4.opExtrude","SWEPT_BODY",BODY,{"disambiguationData":[OSD([sQuery(id+"F0.wireOp",EDGE,"E4"),sQuery(id+"F0.wireOp",EDGE,"E5"),sQuery(id+"F0.wireOp",EDGE,"E6"),sQuery(id+"F0.wireOp",EDGE,"E7"),sQuery(id+"F0.wireOp",EDGE,"E8"),sQuery(id+"F0.wireOp",EDGE,"E10.MirrorCS"),sQuery(id+"F0.wireOp",EDGE,"E11")])]});
            hole(context, id + "F8", {"style" : HoleStyle.C_BORE, "endStyle" : HoleEndStyle.BLIND, "holeDiameter" : 5 * mm, "cBoreDiameter" : 9 * mm, "cBoreDepth" : 3.5 * mm, "holeDepth" : 15 * mm, "isTappedThrough" : true, "tappedDepth" : 12 * mm, "tapClearance" : 3, "startFromSketch" : true, "locations" : qUnion([Q0, Q1]), "scope" : qUnion([Q2, Q3])});
        }
        {
            var Q0;
            Q0=qCreatedBy(makeId("Right.planeOp"),FACE);
            var sketch = newSketch(context, id + "F9", { "sketchPlane" : qUnion([Q0])});
            skLineSegment(sketch, "E42", {"start": v(0, 0) * mm, "end": v(0, 25.93) * mm, "construction": true});
            skSolve(sketch);
        }
    });
